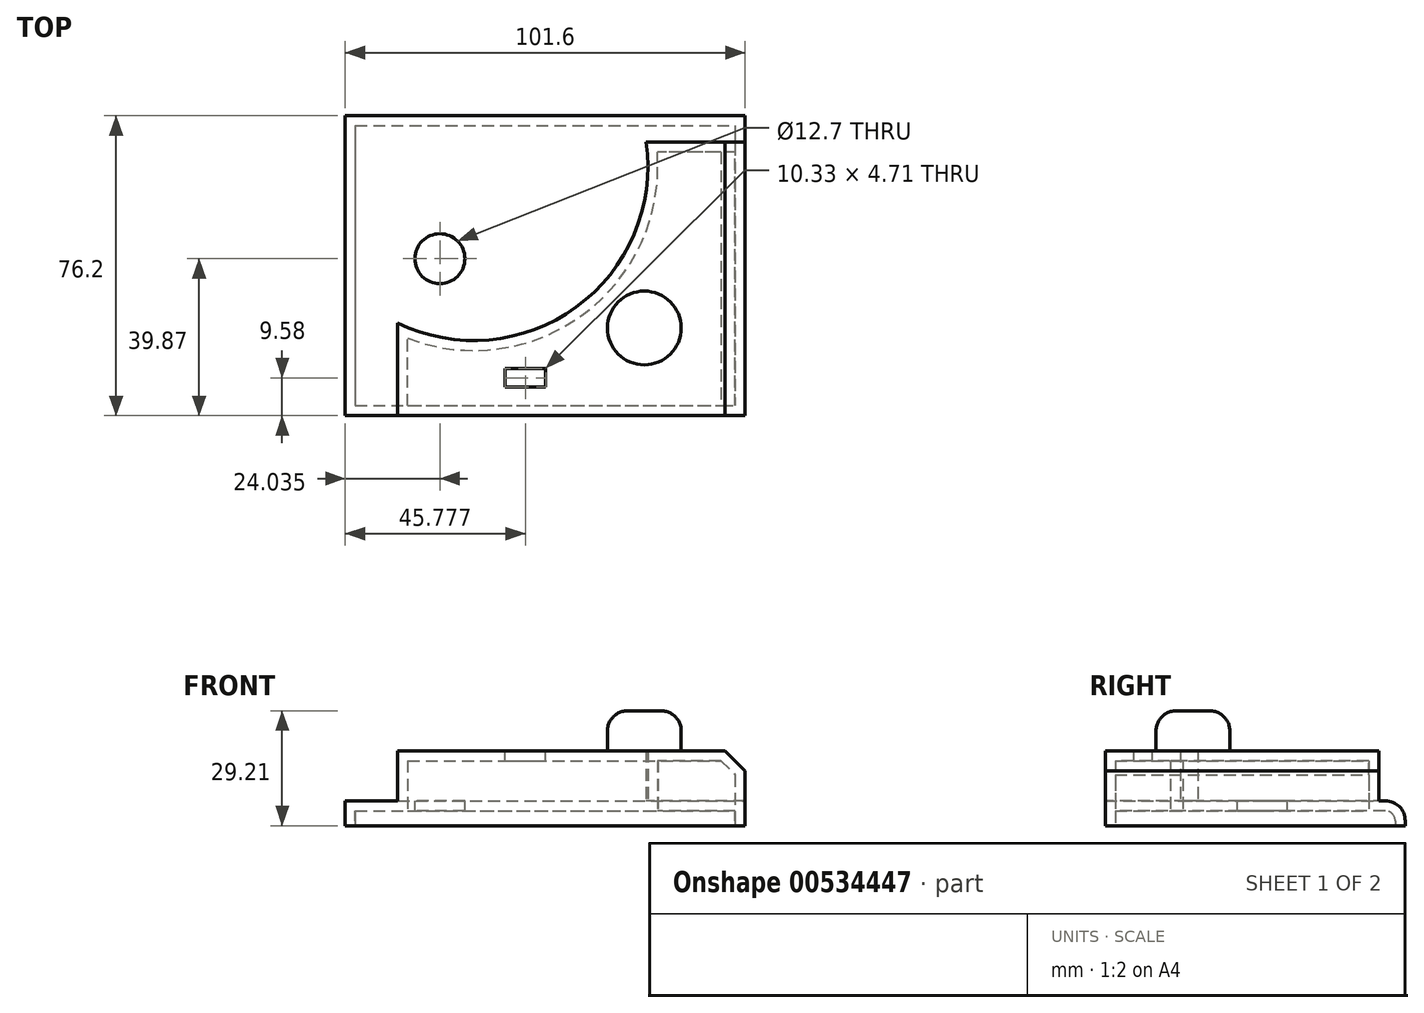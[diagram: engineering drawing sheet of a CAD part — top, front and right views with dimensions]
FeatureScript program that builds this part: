
annotation { "Feature Type Name" : "Feature", "Feature Type Description" : "" }
export const myFeature = defineFeature(function(context is Context, id is Id, definition is map)
    precondition{}
    {
        {
            var Q0;
            Q0=qCreatedBy(makeId("Top.planeOp"),FACE);
            var sketch = newSketch(context, id + "F0", { "sketchPlane" : qUnion([Q0])});
            skLineSegment(sketch, "E0.bottom", {"start": v(-50.94, 36.33) * mm, "end": v(50.66, 36.33) * mm});
            skLineSegment(sketch, "E0.top", {"start": v(-50.94, -39.87) * mm, "end": v(50.66, -39.87) * mm});
            skLineSegment(sketch, "E0.left", {"start": v(-50.94, 36.33) * mm, "end": v(-50.94, -39.87) * mm});
            skLineSegment(sketch, "E0.right", {"start": v(50.66, 36.33) * mm, "end": v(50.66, -39.87) * mm});
            skSolve(sketch);
        }
        {
            var Q0;
            Q0=makeQuery(id+"F0.imprint","IMPRINT",FACE,{"disambiguationData":[TD([[makeQuery(id+"F0.imprint","IMPRINT",EDGE,{"derivedFrom":sQuery(id+"F0.wireOp",EDGE,"E0.bottom")}),-1.0]])]});
            extrude(context, id + "F1", {"entities" : qUnion([Q0]), "depth" : 6.35 * mm, "offsetDistance" : 25.4 * mm});
        }
        {
            var Q0;
            Q0=makeQuery(id+"F1.opExtrude","CAP_FACE",FACE,{"disambiguationData":[OSD([sQuery(id+"F0.wireOp",EDGE,"E0.bottom"),sQuery(id+"F0.wireOp",EDGE,"E0.top"),sQuery(id+"F0.wireOp",EDGE,"E0.left"),sQuery(id+"F0.wireOp",EDGE,"E0.right")])],"isStart":false});
            var sketch = newSketch(context, id + "F2", { "sketchPlane" : qUnion([Q0])});
            skLineSegment(sketch, "E1", {"start": v(-37.61, -39.87) * mm, "end": v(-37.61, -16.34) * mm});
            skLineSegment(sketch, "E2", {"start": v(50.66, 29.58) * mm, "end": v(25.5, 29.58) * mm});
            skArc(sketch, "E3", {"start": v(-37.61, -16.34) * mm, "mid": v(7.72, -12.31) * mm, "end": v(25.5, 29.58) * mm});
            skSolve(sketch);
        }
        {
            var Q0;
            Q0=makeQuery(id+"F1.opExtrude","CAP_FACE",FACE,{"disambiguationData":[OSD([sQuery(id+"F0.wireOp",EDGE,"E0.bottom"),sQuery(id+"F0.wireOp",EDGE,"E0.top"),sQuery(id+"F0.wireOp",EDGE,"E0.left"),sQuery(id+"F0.wireOp",EDGE,"E0.right")])],"isStart":true});
            extrude(context, id + "F3", {"entities" : qUnion([Q0]), "operationType" : NewBodyOperationType.ADD, "oppositeDirection" : true, "depth" : 5.33 * mm, "offsetDistance" : 25.4 * mm});
        }
        {
            var Q0;
            Q0 = qSketchRegion(id + "F2", true);
            var Q1;
            {var subQ3=sQuery(id+"F2.wireOp",EDGE,"E1");Q1=makeQuery(id+"F2.imprint","IMPRINT",FACE,{"disambiguationData":[TD([[makeQuery(id+"F2.imprint","IMPRINT",EDGE,{"derivedFrom":subQ3}),-1.0]])]});}
            extrude(context, id + "F4", {"entities" : qUnion([Q0, Q1]), "operationType" : NewBodyOperationType.ADD, "depth" : 12.7 * mm, "offsetDistance" : 25.4 * mm});
        }
        {
            var Q0;
            Q0=makeQuery(id+"F1.opExtrude","CAP_EDGE",EDGE,{"disambiguationData":[OSD([sQuery(id+"F0.wireOp",EDGE,"E0.bottom")])],"isStart":false});
            fillet(context, id + "F5", {"entities" : qUnion([Q0]), "radius" : 5.08 * mm, "tangentPropagation" : true, "allowEdgeOverflow" : false});
        }
        {
            var Q0;
            Q0=makeQuery(id+"F4.opExtrude","CAP_EDGE",EDGE,{"disambiguationData":[OSD([sQuery(id+"F0.wireOp",EDGE,"E0.right")])],"isStart":false});
            chamfer(context, id + "F6", {"entities" : qUnion([Q0]), "width" : 5.08 * mm, "tangentPropagation" : true});
        }
        {
            var Q0;
            Q0=makeQuery(id+"F1.opExtrude","CAP_FACE",FACE,{"disambiguationData":[OSD([sQuery(id+"F0.wireOp",EDGE,"E0.bottom"),sQuery(id+"F0.wireOp",EDGE,"E0.top"),sQuery(id+"F0.wireOp",EDGE,"E0.left"),sQuery(id+"F0.wireOp",EDGE,"E0.right")])],"isStart":false});
            var sketch = newSketch(context, id + "F7", { "sketchPlane" : qUnion([Q0])});
            skCircle(sketch, "E4", {"center": v(-26.9, 0) * mm, "radius": 8.43 * mm});
            skSolve(sketch);
        }
        {
            var Q0;
            Q0=makeQuery(id+"F1.opExtrude","CAP_FACE",FACE,{"disambiguationData":[OSD([sQuery(id+"F0.wireOp",EDGE,"E0.bottom"),sQuery(id+"F0.wireOp",EDGE,"E0.top"),sQuery(id+"F0.wireOp",EDGE,"E0.left"),sQuery(id+"F0.wireOp",EDGE,"E0.right")])],"isStart":true});
            shell(context, id + "F8", {"entities" : qUnion([Q0]), "thickness" : 2.54 * mm});
        }
        {
            var Q0;
            Q0=sQuery(id+"F7.wireOp",VERTEX,"E4.center");
            var Q1;
            Q1=makeQuery(id+"F1.opExtrude","SWEPT_BODY",BODY,{"disambiguationData":[OSD([sQuery(id+"F0.wireOp",EDGE,"E0.bottom"),sQuery(id+"F0.wireOp",EDGE,"E0.top"),sQuery(id+"F0.wireOp",EDGE,"E0.left"),sQuery(id+"F0.wireOp",EDGE,"E0.right")])]});
            hole(context, id + "F9", {"style" : HoleStyle.SIMPLE, "endStyle" : HoleEndStyle.THROUGH, "holeDiameter" : 12.7 * mm, "isTappedThrough" : true, "tappedDepth" : 12.7 * mm, "tapClearance" : 3, "locations" : qUnion([Q0]), "scope" : qUnion([Q1])});
        }
        {
            var Q0;
            Q0=makeQuery(id+"F4.opExtrude","CAP_FACE",FACE,{"disambiguationData":[OSD([sQuery(id+"F0.wireOp",EDGE,"E0.top"),sQuery(id+"F0.wireOp",EDGE,"E0.right"),sQuery(id+"F2.wireOp",EDGE,"E1"),sQuery(id+"F2.wireOp",EDGE,"E2"),sQuery(id+"F2.wireOp",EDGE,"E3")])],"isStart":false});
            var sketch = newSketch(context, id + "F10", { "sketchPlane" : qUnion([Q0])});
            skCircle(sketch, "E5", {"center": v(25.03, -17.6) * mm, "radius": 9.37 * mm});
            skSolve(sketch);
        }
        {
            var Q0;
            Q0=makeQuery(id+"F10.imprint","IMPRINT",FACE,{"disambiguationData":[TD([[makeQuery(id+"F10.imprint","IMPRINT",EDGE,{"derivedFrom":sQuery(id+"F10.wireOp",EDGE,"E5")}),1.0]])]});
            extrude(context, id + "F11", {"entities" : qUnion([Q0]), "operationType" : NewBodyOperationType.ADD, "depth" : 10.16 * mm, "offsetDistance" : 25.4 * mm});
        }
        {
            var Q0;
            Q0=makeQuery(id+"F11.opExtrude","CAP_FACE",FACE,{"disambiguationData":[OSD([sQuery(id+"F10.wireOp",EDGE,"E5")])],"isStart":false});
            fillet(context, id + "F12", {"entities" : qUnion([Q0]), "radius" : 5.08 * mm, "tangentPropagation" : true, "allowEdgeOverflow" : false});
        }
        {
            var Q0;
            Q0=makeQuery(id+"F4.opExtrude","CAP_FACE",FACE,{"disambiguationData":[OSD([sQuery(id+"F0.wireOp",EDGE,"E0.top"),sQuery(id+"F0.wireOp",EDGE,"E0.right"),sQuery(id+"F2.wireOp",EDGE,"E1"),sQuery(id+"F2.wireOp",EDGE,"E2"),sQuery(id+"F2.wireOp",EDGE,"E3")])],"isStart":false});
            var sketch = newSketch(context, id + "F13", { "sketchPlane" : qUnion([Q0])});
            skLineSegment(sketch, "E6.bottom", {"start": v(-10.33, -27.94) * mm, "end": v(0, -27.94) * mm});
            skLineSegment(sketch, "E6.top", {"start": v(-10.33, -32.64) * mm, "end": v(0, -32.64) * mm});
            skLineSegment(sketch, "E6.left", {"start": v(-10.33, -27.94) * mm, "end": v(-10.33, -32.64) * mm});
            skLineSegment(sketch, "E6.right", {"start": v(0, -27.94) * mm, "end": v(0, -32.64) * mm});
            skSolve(sketch);
        }
        {
            var Q0;
            Q0=makeQuery(id+"F13.imprint","IMPRINT",FACE,{"disambiguationData":[TD([[makeQuery(id+"F13.imprint","IMPRINT",EDGE,{"derivedFrom":sQuery(id+"F13.wireOp",EDGE,"E6.bottom")}),-1.0]])]});
            extrude(context, id + "F14", {"entities" : qUnion([Q0]), "operationType" : NewBodyOperationType.REMOVE, "oppositeDirection" : true, "depth" : 25.4 * mm, "offsetDistance" : 25.4 * mm});
        }
    });
